# Revit family: Unidad de evaluacion D_List_Aguilera Electronica
name_source: partatom
category: Equipos eléctricos
units: mm (PartAtom-declared; Revit-internal decimal feet)

## family parameters
Anfitrión = Cara
Compartido = No
Configuración de panel = Una columna
Corte con vacíos al cargar = No
Cota de conector redondo = Diámetro de uso
Número OmniClass = 23.85.30.21.11.14
Punto de cálculo de habitación = No
Tipo de pieza = Cuadro de control
Título OmniClass = Alarm Panels

## types (1)
- Unidad de evaluación D-List
    Alto = 150 mm  [stored 0.492126 ft]
    Ancho = 260 mm  [stored 0.853018 ft]
    Comentarios de tipo = Evaluación de temperaturas medidas por los cables sensores SEC15 y/o por los sensores externos ESD-A5
Dos entradas para los cables sensores A / B
Disparo de alarma por temperatura diferencial y máxima
Parámetros de respuesta conforme a la EN 54-22, certificado por VdS Schadenverhütung GmbH, VdS Nr. G 221004, grupo medioambiental III
1. como detector de calor de tipo lineal no integrado: A1N, A2N, BN, CN
2. como detector de calor de tipo lineal integrado: A1I, A2I, BI, CI (solicitada a la VdS Schadenverhütung GmbH)
Exclusión de falsas alarmas mediante algoritmos inteligentes de evaluación
Larga vida útil gracias a la utilización de componentes sin mantenimiento conforme a la RoHS
Señalización de alarmas por LEDs en el panel frontal
Muy bajo consumo energético
Hasta 32 zonas programables de 255 posibles, para el reenvío de mensajes de alarma y fallos a los sistemas superiores mediante protocolo
Tipo AECS/DLIST: Alarma de incendio común y relé de fallo común por cada puerto de cable sensor A / B
Tipo AECS/DLIST + Tarjeta relés REL 835: 16 zonas relés, libremente programable para alarmas de incendio, averías o preseñales por sección de cable sensor
configurada.
Salidas de relés configurables con resistencia de bucle de circuito cerrado
Junta de la tapa aprobada contra EMC
Prensaestopas métricos de poliamida con juntas tóricas NBR y sellado con forma
    Descripción = Unidad de evaluación y control de las temperaturas medidas por los cables sensores SEC15 y/o por los sensores externos ESD. Dispone de 2 puertos para 2 líneas de cables sensor de hasta 350m cada una (según configuraciones).
El disparo de la alarma se realiza en función de los datos medidos en uno o varios sensores por temperatura diferencial o por temperatura máxima. Incorpora algoritmos inteligentes de evaluación para la exclusión de falsas alarmas.
La alarma se señaliza tanto ópticamente en el frontal, leds de alarma y avería, como por relés libres de tensión, por cada puerto, así como 2 salidas ópticas para conexión de sirenas, dispositivos acústicos
luminosos o similares.
Ampliación de relés mediante tarjeta AECS/DLISTR835.
Dispone de 4 entradas programables para la programación de funciones especiales como modo día/noche, desactivación del modo diferencial y detección por coincidencia.
Puertos de comunicaciones RS232, RS485. Conexión USB y Ethernet. Protocolo ModBus RTU y TCP/IP incorporado.
La unidad está certificada por VdS según norma EN 54-22
Alimentación +10,5Vcc … +30 Vcc.
Potencia máxima 4,4 W
Consumo máximo 150 mA
Dimensiones 290 X 177 X 91 mm.
Peso 1.95kg
Temperatura de servicio: -25ºC … +70ºC
Envolvente de aluminio pintada en color RAL 7035. Protección: IP 65
    Elevación por defecto = 1200 mm
    Fabricante = Aguilera Electrónica
    Fondo = 90 mm  [stored 0.295276 ft]
    Modelo = AECS/DLIST
    Símbolo = Sí
    Símbolo texto modelo = Sí
    URL = https://aguilera.es
    Voltaje = 2,7 W

note: [stored X ft] marks values corroborated as IEEE doubles in the binary element streams (Revit-internal decimal feet)
